# Revit family: Rough_In_Valve-GROHE-Grohsafe-35066001
name_source: partatom
category: Pipe Accessories
revit_build: Autodesk Revit 2014 (Build: 20130308_1515(x64)
units: mm (PartAtom-declared; Revit-internal decimal feet)

## types (1)
- 35066001
    Assembly Code = D2020
    CW Connection = Yes
    CWFU = 2
    Cold Water Connection Diameter = 1/2"
    Cold Water Connection Radius = 1/4"
    Default Elevation = 0"
    Description = Grohsafe Universal Pressure Balance Rough-In valve
    Flow Rate = (top port) 5.5 gpm at 45 psi (21 l/min), (bottom port) 5.8 gpm at 45 psi (22 l/min)
    HW Connection = Yes
    HWFU = 3
    Height = 4 3/16"
    Hot Water Connection Diameter = 1"
    IAPMO Compliance = cUPC
    Installation Type = Wall Installation
    Manufacturer = GROHE
    Material = Copper-Grohe-000-Brass
    Model = 35066001
    Price = Prices may vary. Please consult Manufacturer Representative for most up-to-date price list.
    Product Page URL = https://www.grohe.us
    Tempered Water Connection Diameter = 1/2"
    URL = https://www.grohe.us
    Vent Connection = No
    WFU = 4
    Warranty Information = Limited Lifetime Warranty
    Waste Connection = No
    Width = 4 1/8"

## geometry (parser evidence)
native form markers: Sweep x1
no freeform markers — native parametric forms only
